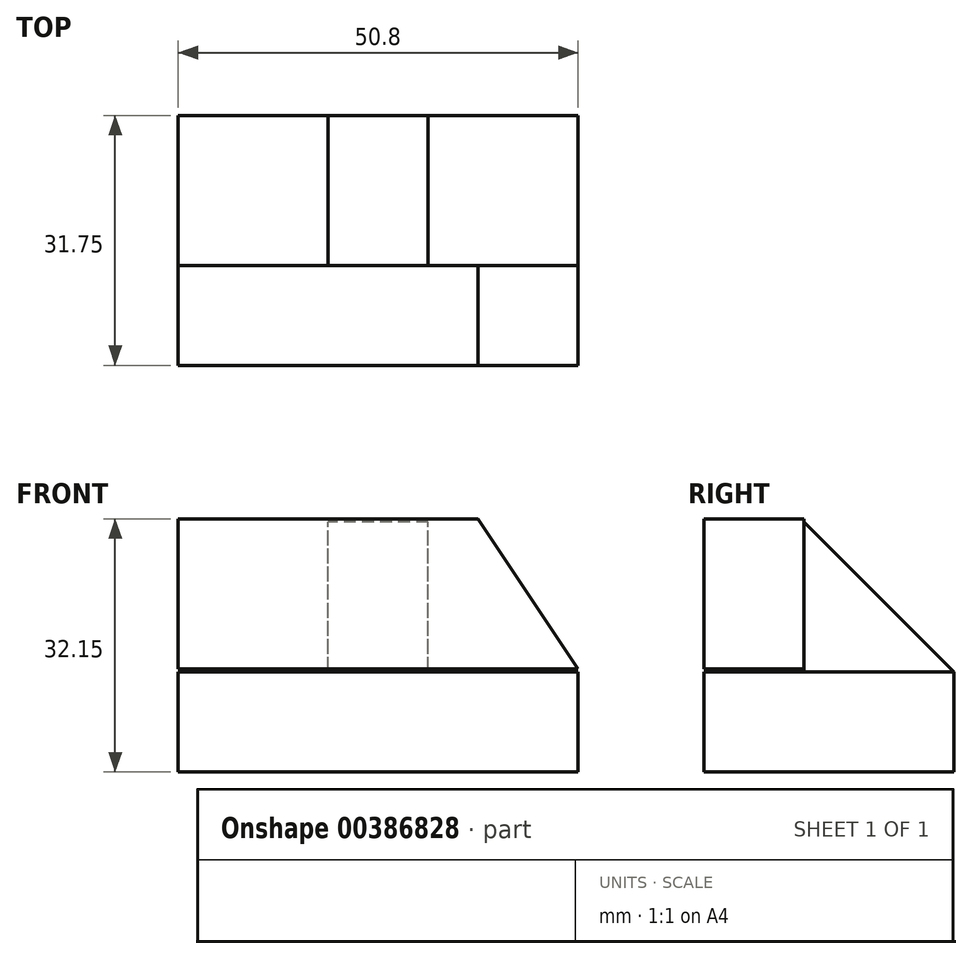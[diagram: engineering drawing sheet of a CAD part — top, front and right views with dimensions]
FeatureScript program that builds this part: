
annotation { "Feature Type Name" : "Feature", "Feature Type Description" : "" }
export const myFeature = defineFeature(function(context is Context, id is Id, definition is map)
    precondition{}
    {
        {
            var Q0;
            Q0=qCreatedBy(makeId("Top.planeOp"),FACE);
            var sketch = newSketch(context, id + "F0", { "sketchPlane" : qUnion([Q0])});
            skLineSegment(sketch, "E0", {"start": v(0, 0) * mm, "end": v(50.8, 0) * mm});
            skLineSegment(sketch, "E1", {"start": v(0, 0) * mm, "end": v(0, 31.75) * mm});
            skLineSegment(sketch, "E2", {"start": v(0, 31.75) * mm, "end": v(50.8, 31.75) * mm});
            skLineSegment(sketch, "E3", {"start": v(50.8, 31.75) * mm, "end": v(50.8, 0) * mm});
            skSolve(sketch);
        }
        {
            var Q0;
            Q0=makeQuery(id+"F0.imprint","IMPRINT",FACE,{"disambiguationData":[TD([[makeQuery(id+"F0.imprint","IMPRINT",EDGE,{"derivedFrom":sQuery(id+"F0.wireOp",EDGE,"E0")}),1.0]])]});
            extrude(context, id + "F1", {"entities" : qUnion([Q0]), "depth" : 12.7 * mm});
        }
        {
            var Q0;
            Q0=qCreatedBy(makeId("Front.planeOp"),FACE);
            var sketch = newSketch(context, id + "F2", { "sketchPlane" : qUnion([Q0])});
            skLineSegment(sketch, "E4", {"start": v(0, 13.1) * mm, "end": v(0, 32.15) * mm});
            skLineSegment(sketch, "E5", {"start": v(0, 32.15) * mm, "end": v(38.1, 32.15) * mm});
            skLineSegment(sketch, "E6", {"start": v(0, 13.1) * mm, "end": v(50.8, 13.1) * mm});
            skLineSegment(sketch, "E7", {"start": v(50.8, 13.1) * mm, "end": v(38.1, 32.15) * mm});
            skSolve(sketch);
        }
        {
            var Q0;
            Q0=makeQuery(id+"F2.imprint","IMPRINT",FACE,{"disambiguationData":[TD([[makeQuery(id+"F2.imprint","IMPRINT",EDGE,{"derivedFrom":sQuery(id+"F2.wireOp",EDGE,"E4")}),-1.0]])]});
            extrude(context, id + "F3", {"entities" : qUnion([Q0]), "oppositeDirection" : true, "depth" : 12.7 * mm});
        }
        {
            var Q0;
            Q0=makeQuery(id+"F1.opExtrude","SWEPT_FACE",FACE,{"disambiguationData":[OSD([sQuery(id+"F0.wireOp",EDGE,"E1")])]});
            var sketch = newSketch(context, id + "F4", { "sketchPlane" : qUnion([Q0])});
            skLineSegment(sketch, "E8", {"start": v(-31.75, 12.7) * mm, "end": v(-12.7, 12.7) * mm});
            skLineSegment(sketch, "E9", {"start": v(-12.7, 12.7) * mm, "end": v(-12.7, 31.75) * mm});
            skLineSegment(sketch, "E10", {"start": v(-31.75, 12.7) * mm, "end": v(-12.7, 31.75) * mm});
            skSolve(sketch);
        }
        {
            var Q0;
            Q0=makeQuery(id+"F4.imprint","IMPRINT",FACE,{"disambiguationData":[TD([[makeQuery(id+"F4.imprint","IMPRINT",EDGE,{"derivedFrom":sQuery(id+"F4.wireOp",EDGE,"E8")}),-1.0]])]});
            extrude(context, id + "F5", {"entities" : qUnion([Q0]), "oppositeDirection" : true, "depth" : 19.05 * mm});
        }
        {
            var Q0;
            Q0=makeQuery(id+"F5.opExtrude","CAP_FACE",FACE,{"disambiguationData":[OSD([sQuery(id+"F4.wireOp",EDGE,"E8"),sQuery(id+"F4.wireOp",EDGE,"E9"),sQuery(id+"F4.wireOp",EDGE,"E10")])],"isStart":false});
            extrude(context, id + "F6", {"entities" : qUnion([Q0]), "depth" : 12.7 * mm});
        }
        {
            var Q0;
            Q0=makeQuery(id+"F5.opExtrude","SWEPT_BODY",BODY,{"disambiguationData":[OSD([sQuery(id+"F4.wireOp",EDGE,"E8"),sQuery(id+"F4.wireOp",EDGE,"E9"),sQuery(id+"F4.wireOp",EDGE,"E10")])]});
            deleteBodies(context, id + "F7", {"entities" : qUnion([Q0])});
        }
    });
